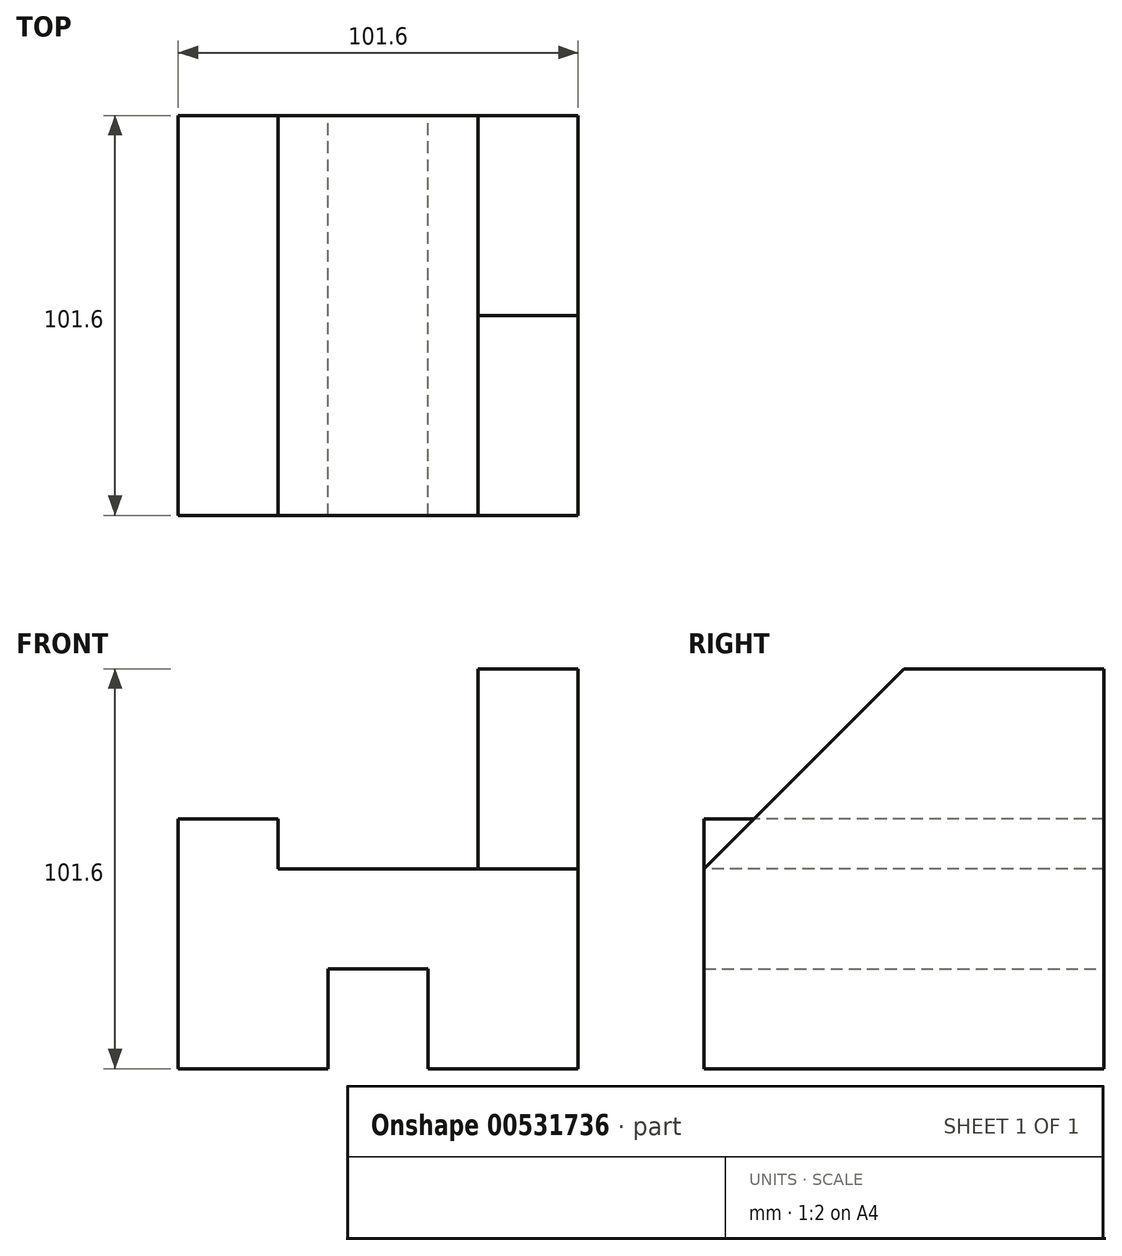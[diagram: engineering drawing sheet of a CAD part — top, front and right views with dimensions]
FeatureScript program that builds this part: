
annotation { "Feature Type Name" : "Feature", "Feature Type Description" : "" }
export const myFeature = defineFeature(function(context is Context, id is Id, definition is map)
    precondition{}
    {
        {
            var Q0;
            Q0=qCreatedBy(makeId("Front.planeOp"),FACE);
            var sketch = newSketch(context, id + "F0", { "sketchPlane" : qUnion([Q0])});
            skLineSegment(sketch, "E0.bottom", {"start": v(-154.32, -86.1) * mm, "end": v(-52.72, -86.1) * mm});
            skLineSegment(sketch, "E0.top", {"start": v(-154.32, 15.5) * mm, "end": v(-52.72, 15.5) * mm});
            skLineSegment(sketch, "E0.left", {"start": v(-154.32, -86.1) * mm, "end": v(-154.32, 15.5) * mm});
            skLineSegment(sketch, "E0.right", {"start": v(-52.72, -86.1) * mm, "end": v(-52.72, 15.5) * mm});
            skSolve(sketch);
        }
        {
            var Q0;
            Q0=makeQuery(id+"F0.imprint","IMPRINT",FACE,{"disambiguationData":[TD([[makeQuery(id+"F0.imprint","IMPRINT",EDGE,{"derivedFrom":sQuery(id+"F0.wireOp",EDGE,"E0.bottom")}),1.0]])]});
            extrude(context, id + "F1", {"entities" : qUnion([Q0]), "depth" : 101.6 * mm, "offsetDistance" : 25.4 * mm});
        }
        {
            var Q0;
            Q0=makeQuery(id+"F1.opExtrude","CAP_FACE",FACE,{"disambiguationData":[OSD([sQuery(id+"F0.wireOp",EDGE,"E0.bottom"),sQuery(id+"F0.wireOp",EDGE,"E0.top"),sQuery(id+"F0.wireOp",EDGE,"E0.left"),sQuery(id+"F0.wireOp",EDGE,"E0.right")])],"isStart":false});
            var sketch = newSketch(context, id + "F2", { "sketchPlane" : qUnion([Q0])});
            skLineSegment(sketch, "E1.bottom", {"start": v(-52.72, 15.5) * mm, "end": v(-78.12, 15.5) * mm});
            skLineSegment(sketch, "E1.top", {"start": v(-52.72, -35.3) * mm, "end": v(-78.12, -35.3) * mm});
            skLineSegment(sketch, "E1.left", {"start": v(-52.72, 15.5) * mm, "end": v(-52.72, -35.3) * mm});
            skLineSegment(sketch, "E1.right", {"start": v(-78.12, 15.5) * mm, "end": v(-78.12, -35.3) * mm});
            skLineSegment(sketch, "E2", {"start": v(-78.12, -35.3) * mm, "end": v(-128.92, -35.3) * mm});
            skLineSegment(sketch, "E3.bottom", {"start": v(-154.32, -86.1) * mm, "end": v(-128.92, -86.1) * mm});
            skLineSegment(sketch, "E3.top", {"start": v(-154.32, -22.6) * mm, "end": v(-128.92, -22.6) * mm});
            skLineSegment(sketch, "E3.left", {"start": v(-154.32, -86.1) * mm, "end": v(-154.32, -22.6) * mm});
            skLineSegment(sketch, "E3.right", {"start": v(-128.92, -86.1) * mm, "end": v(-128.92, -22.6) * mm});
            skSolve(sketch);
        }
        {
            var Q0;
            {var subQ3=sQuery(id+"F2.wireOp",EDGE,"E1.right");Q0=makeQuery(id+"F2.imprint","IMPRINT",FACE,{"disambiguationData":[TD([[makeQuery(id+"F2.imprint","IMPRINT",EDGE,{"derivedFrom":subQ3}),-1.0]])]});}
            extrude(context, id + "F3", {"entities" : qUnion([Q0]), "operationType" : NewBodyOperationType.REMOVE, "oppositeDirection" : true, "depth" : 101.6 * mm, "offsetDistance" : 25.4 * mm});
        }
        {
            var Q0;
            Q0=makeQuery(id+"F1.opExtrude","SWEPT_FACE",FACE,{"disambiguationData":[OSD([sQuery(id+"F0.wireOp",EDGE,"E0.right")])]});
            var sketch = newSketch(context, id + "F4", { "sketchPlane" : qUnion([Q0])});
            skLineSegment(sketch, "E4", {"start": v(-101.6, -35.3) * mm, "end": v(-50.8, 15.5) * mm});
            skSolve(sketch);
        }
        {
            var Q0;
            {var subQ0=sQuery(id+"F4.wireOp",EDGE,"E4");Q0=makeQuery(id+"F4.imprint","IMPRINT",FACE,{"disambiguationData":[TD([[makeQuery(id+"F4.imprint","IMPRINT",EDGE,{"derivedFrom":subQ0}),1.0]])]});}
            extrude(context, id + "F5", {"entities" : qUnion([Q0]), "operationType" : NewBodyOperationType.REMOVE, "oppositeDirection" : true, "depth" : 25.4 * mm, "offsetDistance" : 25.4 * mm});
        }
        {
            var Q0;
            Q0=makeQuery(id+"F1.opExtrude","CAP_FACE",FACE,{"disambiguationData":[OSD([sQuery(id+"F0.wireOp",EDGE,"E0.bottom"),sQuery(id+"F0.wireOp",EDGE,"E0.top"),sQuery(id+"F0.wireOp",EDGE,"E0.left"),sQuery(id+"F0.wireOp",EDGE,"E0.right")])],"isStart":true});
            var sketch = newSketch(context, id + "F6", { "sketchPlane" : qUnion([Q0])});
            skLineSegment(sketch, "E5.bottom", {"start": v(154.32, -86.1) * mm, "end": v(116.22, -86.1) * mm});
            skLineSegment(sketch, "E5.top", {"start": v(154.32, -60.7) * mm, "end": v(116.22, -60.7) * mm});
            skLineSegment(sketch, "E5.left", {"start": v(154.32, -86.1) * mm, "end": v(154.32, -60.7) * mm});
            skLineSegment(sketch, "E5.right", {"start": v(116.22, -86.1) * mm, "end": v(116.22, -60.7) * mm});
            skLineSegment(sketch, "E6.bottom", {"start": v(52.72, -86.1) * mm, "end": v(90.82, -86.1) * mm});
            skLineSegment(sketch, "E6.top", {"start": v(52.72, -60.7) * mm, "end": v(90.82, -60.7) * mm});
            skLineSegment(sketch, "E6.left", {"start": v(52.72, -86.1) * mm, "end": v(52.72, -60.7) * mm});
            skLineSegment(sketch, "E6.right", {"start": v(90.82, -86.1) * mm, "end": v(90.82, -60.7) * mm});
            skLineSegment(sketch, "E7", {"start": v(90.82, -60.7) * mm, "end": v(116.22, -60.7) * mm});
            skSolve(sketch);
        }
        {
            var Q0;
            {var subQ0=sQuery(id+"F6.wireOp",EDGE,"E5.right");Q0=makeQuery(id+"F6.imprint","IMPRINT",FACE,{"disambiguationData":[TD([[makeQuery(id+"F6.imprint","IMPRINT",EDGE,{"derivedFrom":subQ0}),1.0]])]});}
            extrude(context, id + "F7", {"entities" : qUnion([Q0]), "operationType" : NewBodyOperationType.REMOVE, "oppositeDirection" : true, "depth" : 101.6 * mm, "offsetDistance" : 25.4 * mm});
        }
    });
